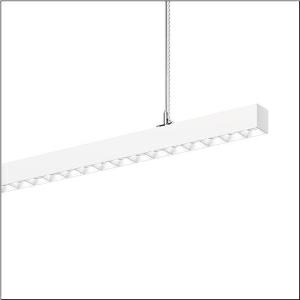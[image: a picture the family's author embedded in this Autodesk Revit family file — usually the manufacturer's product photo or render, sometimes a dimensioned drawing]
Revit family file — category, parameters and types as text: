
# Revit family: silica_r__21_51mx36da37wb_45fb
name_source: partatom
category: Lighting Fixtures
units: mm (PartAtom-declared; Revit-internal decimal feet)

## family parameters
Cut with Voids When Loaded = No
Host = Face
Light Source = No
Part Type = Normal
Room Calculation Point = No
Round Connector Dimension = Use Diameter
Shared = No

## types (1)
- --- (1 x LED, 7060 lm, 43 W, 3000K)
    Apparent Load = 43 VA
    CIE Flux Codes = 83 98 100 61 100
    Color Rendering = 80
    Color Temperature = 3000K
    Default Elevation = 1800 mm
    Description = Silica® 21, office luminaire, primary light control with darklight reflector, of PMMA, white, CAT 2 (L<= 3000cd/m²), light emission: direct/indirect distribution, primary light characteristic: symmetric, installation type: suspended mounting, LED, rated luminous flux: 7.060lm, luminous efficacy: 164lm/W, light colour: 830, colour temperature: 3000K, with terminal, 3+2-pole, max. 2.5mm², mains connection: 220..240V, AC, 50/60Hz, rated input power: 43W, luminaire housing, of aluminium, traffic white (RAL 9016), length: 1.204mm, width: 53mm, height: 53mm, protection rating (complete): IP20, insulation class (complete): insulation class I (protective earthing), certification: CE, permissible operating ambient temperature: 0..+35°C, standard: EN 50419, packaging unit: 1 piece
    Height = 53 mm
    Lamp = 1 x LED
    Lamp Light Flux = 7060 lm
    Lamp Power = 43 W
    Lamp count = 1
    Length = 1204 mm
    Luminous efficacy = 164 lm/W
    Manufacturer = Siteco
    ModVariant = No
    Model = 51MX36DA37WB
    Mounting Place = Ceiling
    Mounting Type = Pendant
    Number of Poles = 1
    OnlyDefault = Yes
    Power Factor = 1
    Product Name = Silica® 21
    Product group = office luminaire | ceiling pendant
    ProductGroupID = 902
    Protection Class = Protection class I
    Protection Degree = IP 20
    RLX_Detail_Level = 1
    RLX_Emergency_Light_Flux = 0 lm
    RLX_Emergency_Type = 0
    RLX_Emergency_Type_DB = No
    RlxData = <blob elided: 40769 chars, md5=b8aa83c1>
    Socket = socket
    Standby Power = 0 W
    System Light Flux = 7060 lm
    System Power = 43 W
    Type Comments = factory setting: luminous flux: 100 % | dim-lin: 254 | 359 mA
    Type Image = l_1297797.jpg
    URL = http://relux.com
    VarID = @adj_052049
    Voltage = 0 V
    Weight = 0.00 kg
    Width = 53 mm

## geometry (parser evidence)
native form markers: Blend x4, Sweep x11
no freeform markers — native parametric forms only
